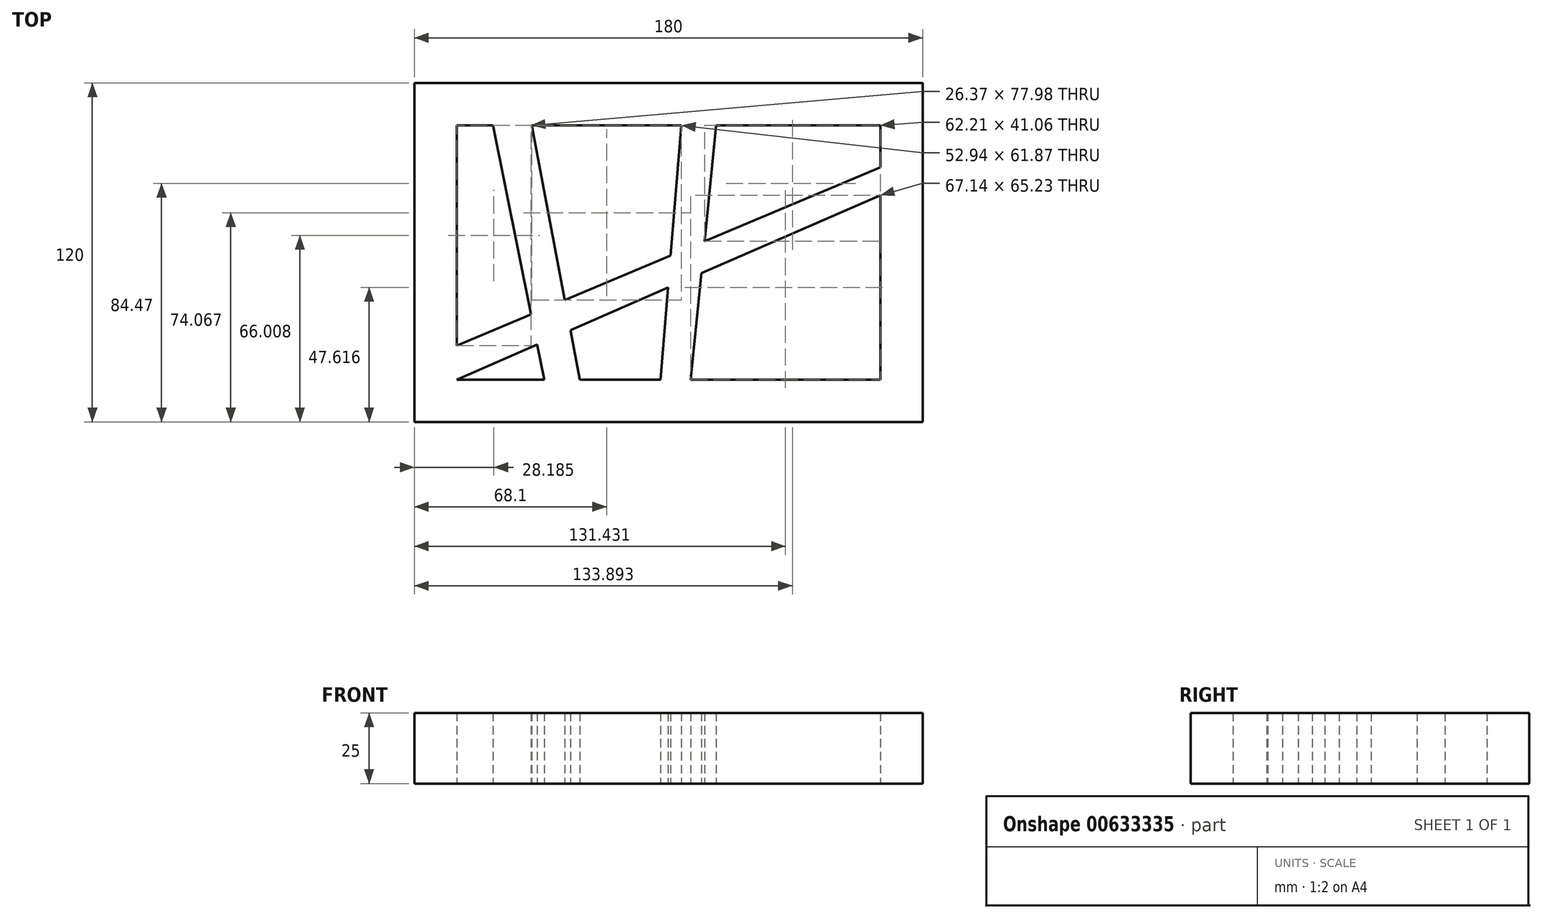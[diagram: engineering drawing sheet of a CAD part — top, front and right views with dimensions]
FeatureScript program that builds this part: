
annotation { "Feature Type Name" : "Feature", "Feature Type Description" : "" }
export const myFeature = defineFeature(function(context is Context, id is Id, definition is map)
    precondition{}
    {
        {
            var Q0;
            Q0=qCreatedBy(makeId("Top.planeOp"),FACE);
            var sketch = newSketch(context, id + "F0", { "sketchPlane" : qUnion([Q0])});
            skLineSegment(sketch, "E0.bottom", {"start": v(90, 60) * mm, "end": v(-90, 60) * mm});
            skLineSegment(sketch, "E0.top", {"start": v(90, -60) * mm, "end": v(-90, -60) * mm});
            skLineSegment(sketch, "E0.left", {"start": v(90, 60) * mm, "end": v(90, -60) * mm});
            skLineSegment(sketch, "E0.right", {"start": v(-90, 60) * mm, "end": v(-90, -60) * mm});
            skPoint(sketch, "E0.middle", {"position": v(0, 0) * mm});
            skLineSegment(sketch, "E1.0", {"start": v(75, 45) * mm, "end": v(16.92, 45) * mm});
            skLineSegment(sketch, "E1.1", {"start": v(75, 45) * mm, "end": v(75, 30.1) * mm});
            skLineSegment(sketch, "E1.2", {"start": v(75, -45) * mm, "end": v(7.86, -45) * mm});
            skLineSegment(sketch, "E1.3", {"start": v(-75, 45) * mm, "end": v(-75, -32.98) * mm});
            skLineSegment(sketch, "E2", {"start": v(-62.09, 45) * mm, "end": v(-48.63, -21.9) * mm});
            skLineSegment(sketch, "E3", {"start": v(-48.37, 45) * mm, "end": v(-36.68, -16.87) * mm});
            skLineSegment(sketch, "E4.trimOffspring", {"start": v(-62.09, 45) * mm, "end": v(-75, 45) * mm});
            skLineSegment(sketch, "E5.trimOffspring", {"start": v(-43.98, -45) * mm, "end": v(-75, -45) * mm});
            skLineSegment(sketch, "E6", {"start": v(-2.84, -45) * mm, "end": v(-0.16, -12.45) * mm});
            skLineSegment(sketch, "E7", {"start": v(16.92, 45) * mm, "end": v(12.79, 3.94) * mm});
            skLineSegment(sketch, "E8.trimOffspring", {"start": v(4.57, 45) * mm, "end": v(-48.37, 45) * mm});
            skLineSegment(sketch, "E9.trimOffspring", {"start": v(-2.84, -45) * mm, "end": v(-31.36, -45) * mm});
            skLineSegment(sketch, "E10", {"start": v(-75, -32.98) * mm, "end": v(-48.63, -21.9) * mm});
            skLineSegment(sketch, "E11", {"start": v(-75, -45) * mm, "end": v(-46.48, -32.6) * mm});
            skLineSegment(sketch, "E12.trimOffspring", {"start": v(75, 20.23) * mm, "end": v(75, -45) * mm});
            skLineSegment(sketch, "E13.trimOffspring", {"start": v(11.65, -7.32) * mm, "end": v(7.86, -45) * mm});
            skLineSegment(sketch, "E14.trimOffspring", {"start": v(12.79, 3.94) * mm, "end": v(75, 30.1) * mm});
            skLineSegment(sketch, "E15.trimOffspring", {"start": v(0.78, -1.11) * mm, "end": v(4.57, 45) * mm});
            skLineSegment(sketch, "E16.trimOffspring", {"start": v(11.65, -7.32) * mm, "end": v(75, 20.23) * mm});
            skLineSegment(sketch, "E17.trimOffspring", {"start": v(-34.68, -27.46) * mm, "end": v(-31.36, -45) * mm});
            skLineSegment(sketch, "E18.trimOffspring", {"start": v(-36.68, -16.87) * mm, "end": v(0.78, -1.11) * mm});
            skLineSegment(sketch, "E19.trimOffspring", {"start": v(-46.48, -32.6) * mm, "end": v(-43.98, -45) * mm});
            skLineSegment(sketch, "E20.trimOffspring", {"start": v(-34.68, -27.46) * mm, "end": v(-0.16, -12.45) * mm});
            skSolve(sketch);
        }
        {
            var Q0;
            Q0 = qSketchRegion(id + "F0", true);
            extrude(context, id + "F1", {"entities" : qUnion([Q0]), "depth" : 25 * mm, "offsetDistance" : 25 * mm});
        }
    });
